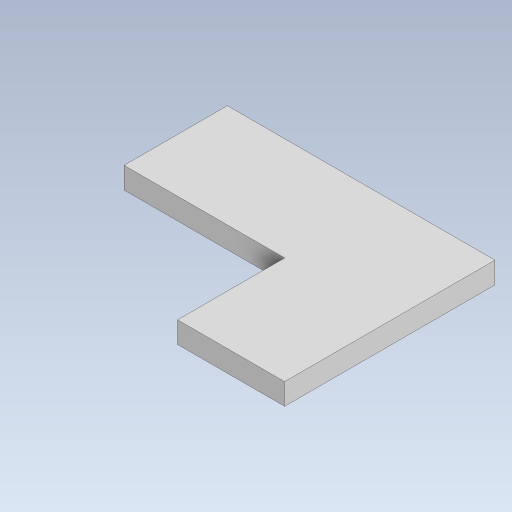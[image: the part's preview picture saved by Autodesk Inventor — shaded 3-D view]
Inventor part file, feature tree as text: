
AUTODESK INVENTOR PART (.ipt)
format: ipt  version: 2023.5 (Build 275446000, 446)  size: 88,064 bytes
history: native  units: in
note: dims shown in document units (in); Inventor stores cm internally (conversion verified against a paired STEP export)
features: extrude x1, sketch x1
ambient origin geometry x8: Origin, YZ Plane, XZ Plane, XY Plane, X Axis, Y Axis, Z Axis, Center Point
bodies: Solid1 (feature_tree)
feature tree (2):
  extrude  "Extrusion1"  Depth=1.5472in
  sketch  "Sketch1"  dims[d0=1.9685in d1=1.5472in d2=1.1811in d3=0.7874in d4=0.1575in d5=0.0in]
